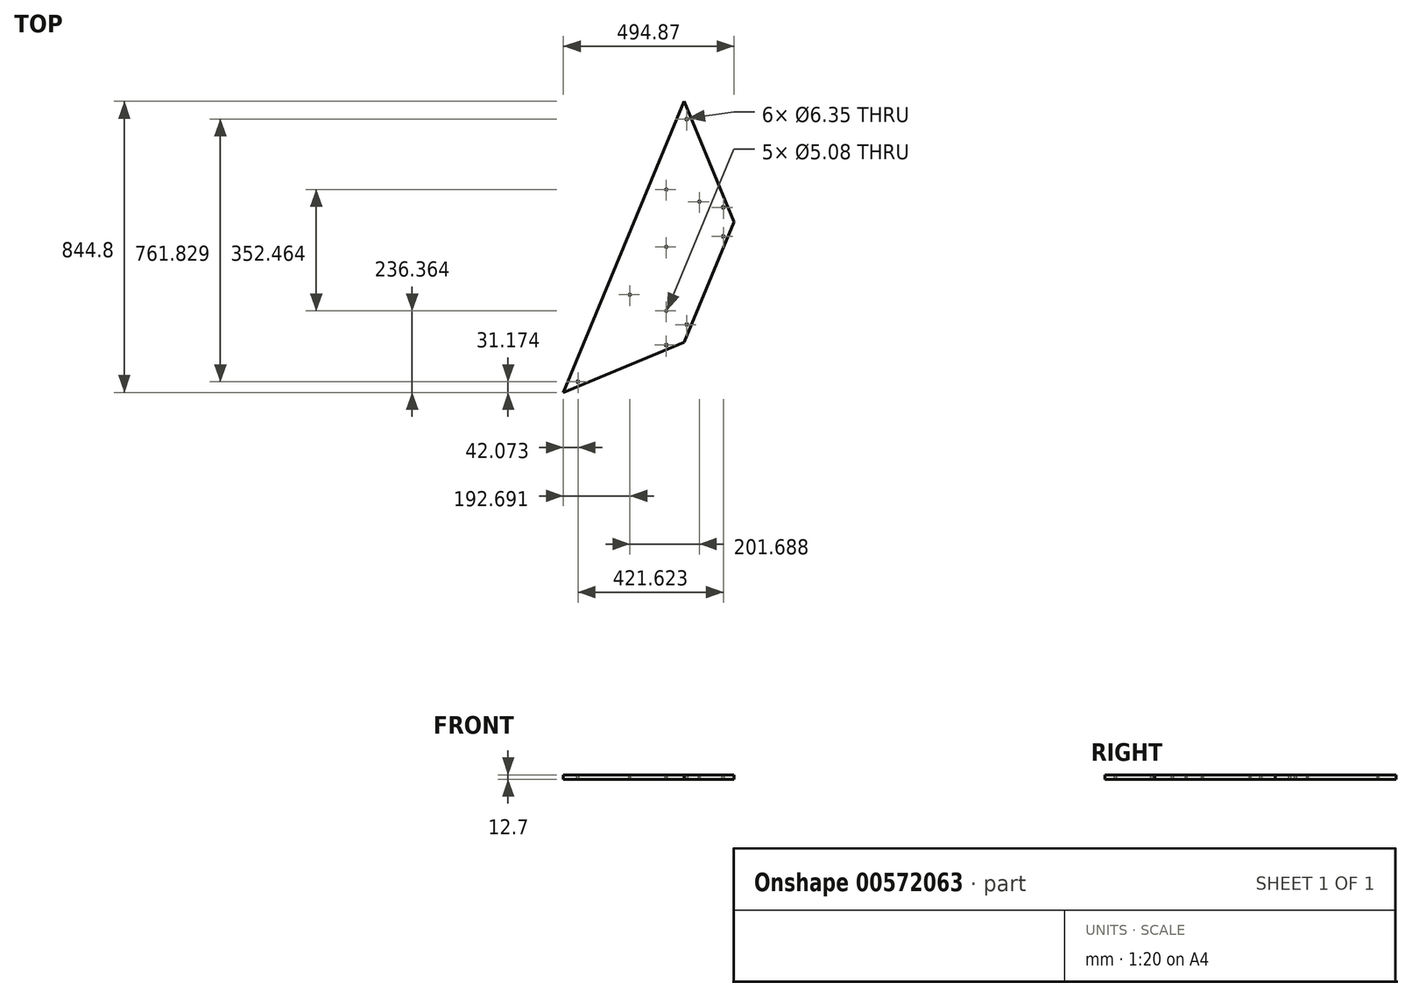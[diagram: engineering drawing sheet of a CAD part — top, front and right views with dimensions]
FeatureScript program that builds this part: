
annotation { "Feature Type Name" : "Feature", "Feature Type Description" : "" }
export const myFeature = defineFeature(function(context is Context, id is Id, definition is map)
    precondition{}
    {
        {
            var Q0;
            Q0=qCreatedBy(makeId("Top.planeOp"),FACE);
            var sketch = newSketch(context, id + "F0", { "sketchPlane" : qUnion([Q0])});
            skCircle(sketch, "E0.cCircle", {"center": v(0, 0) * mm, "radius": 494.87 * mm, "construction": true});
            skLineSegment(sketch, "E0.0", {"start": v(494.87, 0) * mm, "end": v(349.93, -349.93) * mm});
            skLineSegment(sketch, "E0.1", {"start": v(349.93, -349.93) * mm, "end": v(0, -494.87) * mm});
            skLineSegment(sketch, "E0.2", {"start": v(0, -494.87) * mm, "end": v(-349.93, -349.93) * mm});
            skLineSegment(sketch, "E0.3", {"start": v(-349.93, -349.93) * mm, "end": v(-494.87, 0) * mm});
            skLineSegment(sketch, "E0.4", {"start": v(-494.87, 0) * mm, "end": v(-349.93, 349.93) * mm});
            skLineSegment(sketch, "E0.5", {"start": v(-349.93, 349.93) * mm, "end": v(0, 494.87) * mm});
            skLineSegment(sketch, "E0.6", {"start": v(0, 494.87) * mm, "end": v(349.93, 349.93) * mm});
            skLineSegment(sketch, "E0.7", {"start": v(349.93, 349.93) * mm, "end": v(494.87, 0) * mm});
            skLineSegment(sketch, "E1", {"start": v(349.93, 349.93) * mm, "end": v(0, -494.87) * mm});
            skSolve(sketch);
        }
        {
            var Q0;
            Q0=makeQuery(id+"F0.imprint","IMPRINT",FACE,{"disambiguationData":[TD([[makeQuery(id+"F0.imprint","IMPRINT",EDGE,{"derivedFrom":sQuery(id+"F0.wireOp",EDGE,"E0.0")}),-1.0]])]});
            extrude(context, id + "F1", {"entities" : qUnion([Q0]), "depth" : 12.7 * mm, "offsetDistance" : 25.4 * mm});
        }
        {
            var Q0;
            Q0=makeQuery(id+"F1.opExtrude","CAP_FACE",FACE,{"disambiguationData":[OSD([sQuery(id+"F0.wireOp",EDGE,"E0.0"),sQuery(id+"F0.wireOp",EDGE,"E0.1"),sQuery(id+"F0.wireOp",EDGE,"E0.7"),sQuery(id+"F0.wireOp",EDGE,"E1")])],"isStart":false});
            var sketch = newSketch(context, id + "F2", { "sketchPlane" : qUnion([Q0])});
            skCircle(sketch, "E2", {"center": v(357.63, 298.13) * mm, "radius": 3.18 * mm});
            skLineSegment(sketch, "E3", {"start": v(357.63, 298.13) * mm, "end": v(354.9, 299.75) * mm});
            skLineSegment(sketch, "E4", {"start": v(357.63, 298.13) * mm, "end": v(369.37, 303) * mm});
            skCircle(sketch, "E5", {"center": v(463.7, 42.07) * mm, "radius": 3.17 * mm});
            skCircle(sketch, "E6", {"center": v(463.7, -42.07) * mm, "radius": 3.18 * mm});
            skCircle(sketch, "E7", {"center": v(357.63, -298.13) * mm, "radius": 3.17 * mm});
            skCircle(sketch, "E8", {"center": v(298.13, -357.63) * mm, "radius": 3.17 * mm});
            skCircle(sketch, "E9", {"center": v(42.07, -463.7) * mm, "radius": 3.18 * mm});
            skLineSegment(sketch, "E10", {"start": v(42.07, -463.7) * mm, "end": v(43.29, -460.76) * mm});
            skLineSegment(sketch, "E11", {"start": v(298.13, -357.63) * mm, "end": v(298.13, -354.46) * mm});
            skLineSegment(sketch, "E12", {"start": v(357.63, -298.13) * mm, "end": v(357.63, -294.96) * mm});
            skLineSegment(sketch, "E13", {"start": v(463.7, -42.07) * mm, "end": v(463.7, -38.9) * mm});
            skLineSegment(sketch, "E14", {"start": v(463.7, 45.25) * mm, "end": v(463.7, 42.07) * mm});
            skLineSegment(sketch, "E15", {"start": v(463.7, 42.07) * mm, "end": v(475.43, 46.93) * mm});
            skLineSegment(sketch, "E16", {"start": v(298.13, -357.63) * mm, "end": v(303, -369.37) * mm});
            skLineSegment(sketch, "E17", {"start": v(42.07, -463.7) * mm, "end": v(46.93, -475.43) * mm});
            skLineSegment(sketch, "E18", {"start": v(357.63, -298.13) * mm, "end": v(369.37, -303) * mm});
            skLineSegment(sketch, "E19", {"start": v(463.7, -42.07) * mm, "end": v(475.43, -46.93) * mm});
            skSolve(sketch);
        }
        {
            var Q0;
            Q0 = qSketchRegion(id + "F2", true);
            extrude(context, id + "F3", {"entities" : qUnion([Q0]), "operationType" : NewBodyOperationType.REMOVE, "endBound" : BoundingType.THROUGH_ALL, "oppositeDirection" : true, "depth" : 25.4 * mm, "offsetDistance" : 25.4 * mm});
        }
        {
            var Q0;
            Q0=makeQuery(id+"F1.opExtrude","CAP_FACE",FACE,{"disambiguationData":[OSD([sQuery(id+"F0.wireOp",EDGE,"E0.0"),sQuery(id+"F0.wireOp",EDGE,"E0.1"),sQuery(id+"F0.wireOp",EDGE,"E0.7"),sQuery(id+"F0.wireOp",EDGE,"E1")])],"isStart":false});
            var sketch = newSketch(context, id + "F4", { "sketchPlane" : qUnion([Q0])});
            skPoint(sketch, "E20", {"position": v(282.87, 188.04) * mm});
            skPoint(sketch, "E21", {"position": v(298.43, 93.96) * mm});
            skPoint(sketch, "E22", {"position": v(394.38, 58.71) * mm});
            skPoint(sketch, "E23", {"position": v(298.43, -258.5) * mm});
            skPoint(sketch, "E24", {"position": v(298.43, -72.48) * mm});
            skPoint(sketch, "E25", {"position": v(192.7, -211.51) * mm});
            skSolve(sketch);
        }
        {
            var Q0;
            Q0=sQuery(id+"F4.wireOp",VERTEX,"E21");
            var Q1;
            Q1=sQuery(id+"F4.wireOp",VERTEX,"E22");
            var Q2;
            Q2=sQuery(id+"F4.wireOp",VERTEX,"E24");
            var Q3;
            Q3=sQuery(id+"F4.wireOp",VERTEX,"E25");
            var Q4;
            Q4=sQuery(id+"F4.wireOp",VERTEX,"E23");
            var Q5;
            Q5=makeQuery(id+"F1.opExtrude","SWEPT_BODY",BODY,{"disambiguationData":[OSD([sQuery(id+"F0.wireOp",EDGE,"E0.0"),sQuery(id+"F0.wireOp",EDGE,"E0.1"),sQuery(id+"F0.wireOp",EDGE,"E0.7"),sQuery(id+"F0.wireOp",EDGE,"E1")])]});
            hole(context, id + "F5", {"style" : HoleStyle.SIMPLE, "endStyle" : HoleEndStyle.THROUGH, "holeDiameter" : 5.08 * mm, "majorDiameter" : 6.35 * mm, "isTappedThrough" : true, "tappedDepth" : 12.7 * mm, "tapClearance" : 3, "locations" : qUnion([Q0, Q1, Q2, Q3, Q4]), "scope" : qUnion([Q5])});
        }
    });
